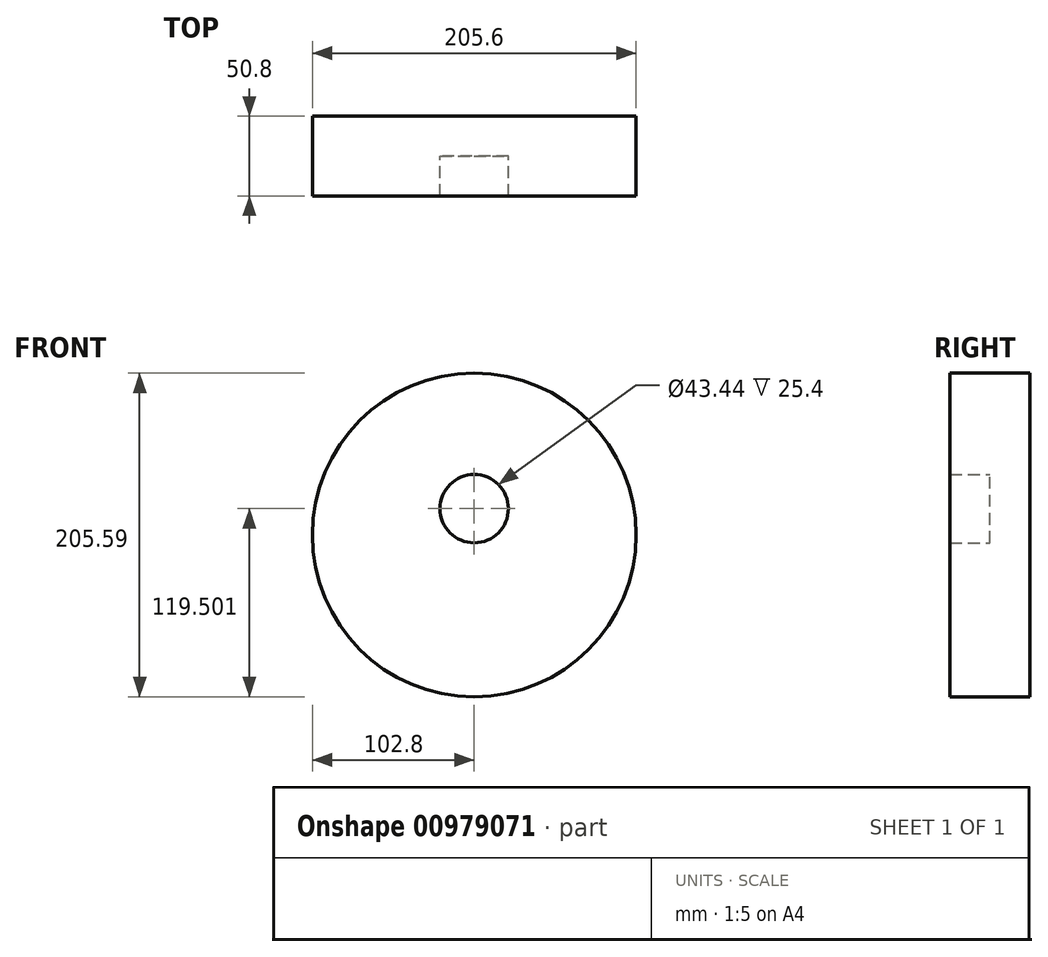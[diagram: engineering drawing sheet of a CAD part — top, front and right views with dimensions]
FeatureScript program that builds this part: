
annotation { "Feature Type Name" : "Feature", "Feature Type Description" : "" }
export const myFeature = defineFeature(function(context is Context, id is Id, definition is map)
    precondition{}
    {
        {
            var Q0;
            Q0=qCreatedBy(makeId("Front.planeOp"),FACE);
            var sketch = newSketch(context, id + "F0", { "sketchPlane" : qUnion([Q0])});
            skCircle(sketch, "E0", {"center": v(0, 39.55) * mm, "radius": 102.8 * mm});
            skLineSegment(sketch, "E1", {"start": v(-81.55, -139.44) * mm, "end": v(108.44, -139.44) * mm});
            skSolve(sketch);
        }
        {
            var Q0;
            Q0=makeQuery(id+"F0.imprint","IMPRINT",FACE,{"disambiguationData":[TD([[makeQuery(id+"F0.imprint","IMPRINT",EDGE,{"derivedFrom":sQuery(id+"F0.wireOp",EDGE,"E0")}),1.0]])]});
            var sketch = newSketch(context, id + "F1", { "sketchPlane" : qUnion([Q0])});
            skArc(sketch, "E2", {"start": v(-64.5, 77.42) * mm, "mid": v(1.01, -28.95) * mm, "end": v(55.9, 83.28) * mm});
            skSolve(sketch);
        }
        {
            var Q0;
            Q0 = qSketchRegion(id + "F1", true);
            var Q1;
            Q1=makeQuery(id+"F0.imprint","IMPRINT",FACE,{"disambiguationData":[TD([[makeQuery(id+"F0.imprint","IMPRINT",EDGE,{"derivedFrom":sQuery(id+"F0.wireOp",EDGE,"E0")}),1.0]])]});
            extrude(context, id + "F2", {"entities" : qUnion([Q0, Q1]), "depth" : 25.4 * mm, "offsetDistance" : 25.4 * mm});
        }
        {
            var Q0;
            Q0=makeQuery(id+"F2.opExtrude","CAP_FACE",FACE,{"disambiguationData":[OSD([sQuery(id+"F0.wireOp",EDGE,"E0")])],"isStart":false});
            var sketch = newSketch(context, id + "F3", { "sketchPlane" : qUnion([Q0])});
            skCircle(sketch, "E3", {"center": v(0, 56.26) * mm, "radius": 21.72 * mm});
            skSolve(sketch);
        }
        {
            var Q0;
            Q0=makeQuery(id+"F3.imprint","IMPRINT",FACE,{"disambiguationData":[TD([[makeQuery(id+"F3.imprint","IMPRINT",EDGE,{"derivedFrom":sQuery(id+"F3.wireOp",EDGE,"E3")}),-1.0]])]});
            extrude(context, id + "F4", {"entities" : qUnion([Q0]), "operationType" : NewBodyOperationType.ADD, "depth" : 25.4 * mm, "offsetDistance" : 25.4 * mm});
        }
    });
